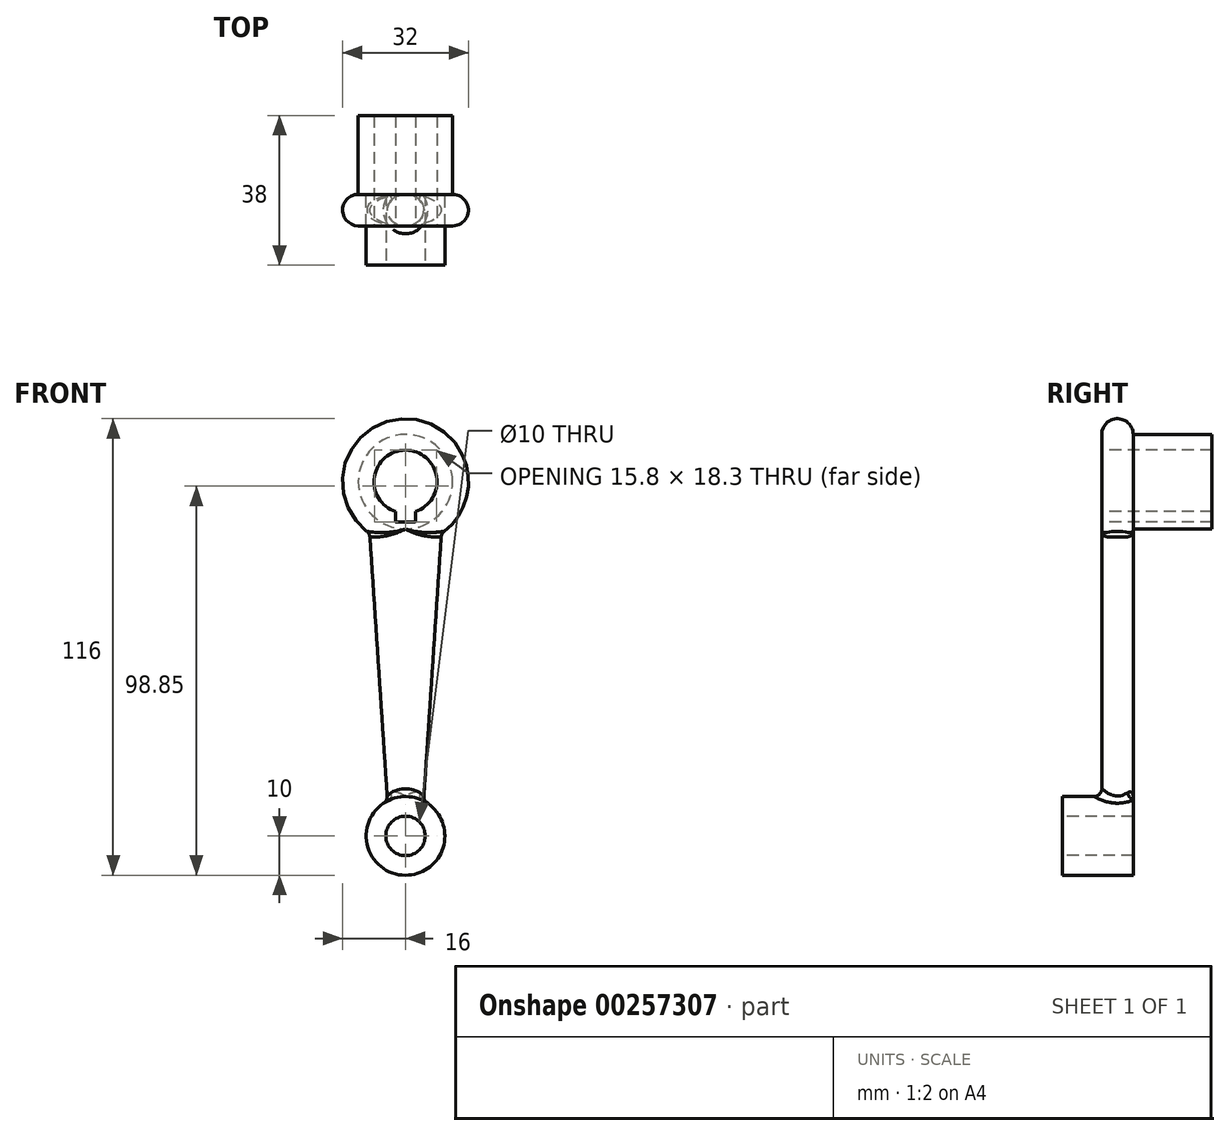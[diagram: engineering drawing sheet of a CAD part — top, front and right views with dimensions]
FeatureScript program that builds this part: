
annotation { "Feature Type Name" : "Feature", "Feature Type Description" : "" }
export const myFeature = defineFeature(function(context is Context, id is Id, definition is map)
    precondition{}
    {
        {
            var Q0;
            Q0=qCreatedBy(makeId("Right.planeOp"),FACE);
            var sketch = newSketch(context, id + "F0", { "sketchPlane" : qUnion([Q0])});
            skLineSegment(sketch, "E0", {"start": v(0, 8) * mm, "end": v(28, 8) * mm, "construction": true});
            skLineSegment(sketch, "E1", {"start": v(28, 8) * mm, "end": v(28, 12) * mm});
            skLineSegment(sketch, "E2", {"start": v(28, 12) * mm, "end": v(8, 12) * mm});
            skLineSegment(sketch, "E3", {"start": v(0, 12) * mm, "end": v(0, 8) * mm});
            skArc(sketch, "E4", {"start": v(0, 12) * mm, "mid": v(4, 16) * mm, "end": v(8, 12) * mm});
            skLineSegment(sketch, "E5", {"start": v(-3.82, 0) * mm, "end": v(31.7, 0) * mm, "construction": true});
            skLineSegment(sketch, "E6", {"start": v(0, 8) * mm, "end": v(0, 0) * mm});
            skLineSegment(sketch, "E7", {"start": v(0, 0) * mm, "end": v(28, 0) * mm});
            skLineSegment(sketch, "E8", {"start": v(28, 0) * mm, "end": v(28, 8) * mm});
            skSolve(sketch);
        }
        {
            var Q0;
            Q0=makeQuery(id+"F0.imprint","IMPRINT",FACE,{"disambiguationData":[TD([[makeQuery(id+"F0.imprint","IMPRINT",EDGE,{"derivedFrom":sQuery(id+"F0.wireOp",EDGE,"E1")}),1.0]])]});
            var Q1;
            Q1=sQuery(id+"F0.wireOp",EDGE,"E5");
            revolve(context, id + "F1", {"entities" : qUnion([Q0]), "axis" : qUnion([Q1]), "revolveType" : RevolveType.FULL});
        }
        {
            var Q0;
            Q0=qCreatedBy(makeId("Front.planeOp"),FACE);
            var sketch = newSketch(context, id + "F2", { "sketchPlane" : qUnion([Q0])});
            skCircle(sketch, "E9", {"center": v(0, -90) * mm, "radius": 10 * mm});
            skSolve(sketch);
        }
        {
            var Q0;
            Q0=makeQuery(id+"F2.imprint","IMPRINT",FACE,{"disambiguationData":[TD([[makeQuery(id+"F2.imprint","IMPRINT",EDGE,{"derivedFrom":sQuery(id+"F2.wireOp",EDGE,"E9")}),1.0]])]});
            extrude(context, id + "F3", {"entities" : qUnion([Q0]), "depth" : 10 * mm, "hasSecondDirection" : true, "secondDirectionOppositeDirection" : true, "secondDirectionDepth" : 8 * mm});
        }
        {
            var Q0;
            Q0=qCreatedBy(makeId("Front.planeOp"),FACE);
            cPlane(context, id + "F4", {"entities" : qUnion([Q0]), "cplaneType" : CPlaneType.OFFSET, "offset" : 4 * mm, "oppositeDirection" : true, "width" : 150 * mm, "height" : 150 * mm});
        }
        {
            var Q0;
            Q0=qCreatedBy(id+"F4.planeOp",FACE);
            var sketch = newSketch(context, id + "F5", { "sketchPlane" : qUnion([Q0])});
            skLineSegment(sketch, "E10", {"start": v(10, 0) * mm, "end": v(4, -90) * mm, "construction": true});
            skLineSegment(sketch, "E11.MirrorCS", {"start": v(-10, 0) * mm, "end": v(-4, -90) * mm, "construction": true});
            skCircle(sketch, "E12.0", {"center": v(0, -90) * mm, "radius": 10 * mm});
            skSolve(sketch);
        }
        {
            var Q0;
            Q0=qCreatedBy(makeId("Top.planeOp"),FACE);
            cPlane(context, id + "F6", {"entities" : qUnion([Q0]), "cplaneType" : CPlaneType.OFFSET, "offset" : 90 * mm, "oppositeDirection" : true, "width" : 150 * mm, "height" : 150 * mm});
        }
        {
            var Q0;
            Q0=qCreatedBy(makeId("Top.planeOp"),FACE);
            var sketch = newSketch(context, id + "F7", { "sketchPlane" : qUnion([Q0])});
            skPoint(sketch, "E13.0", {"position": v(10, 4) * mm});
            skPoint(sketch, "E13.1", {"position": v(-10, 4) * mm});
            skPoint(sketch, "E14.0", {"position": v(0, 4) * mm});
            skEllipse(sketch, "E15", {"center": v(0, 4) * mm, "majorRadius": 10 * mm, "minorRadius": 4 * mm, "majorAxis": v(1, 0)});
            skSolve(sketch);
        }
        {
            var Q0;
            Q0=qCreatedBy(id+"F6.planeOp",FACE);
            var sketch = newSketch(context, id + "F8", { "sketchPlane" : qUnion([Q0])});
            skPoint(sketch, "E16.0", {"position": v(0, 4) * mm});
            skPoint(sketch, "E16.1", {"position": v(-4, 4) * mm});
            skPoint(sketch, "E16.2", {"position": v(4, 4) * mm});
            skEllipse(sketch, "E17", {"center": v(0, 4) * mm, "majorRadius": 4 * mm, "minorRadius": 4 * mm, "majorAxis": v(-1, 0)});
            skSolve(sketch);
        }
        {
            var Q0;
            Q0 = qSketchRegion(id + "F7", true);
            var Q1;
            Q1 = qSketchRegion(id + "F8", true);
            loft(context, id + "F9", {"sheetProfilesArray" : [{ "sheetProfileEntities" : qUnion([Q0]) }, { "sheetProfileEntities" : qUnion([Q1]) }]});
        }
        {
            var Q0;
            Q0=makeQuery(id+"F1.opRevolve","SWEPT_BODY",BODY,{"disambiguationData":[OSD([sQuery(id+"F0.wireOp",EDGE,"E1"),sQuery(id+"F0.wireOp",EDGE,"E2"),sQuery(id+"F0.wireOp",EDGE,"E3"),sQuery(id+"F0.wireOp",EDGE,"E4"),sQuery(id+"F0.wireOp",EDGE,"E6"),sQuery(id+"F0.wireOp",EDGE,"E7"),sQuery(id+"F0.wireOp",EDGE,"E8")])]});
            var Q1;
            Q1=makeQuery(id+"F9.opLoft","SWEPT_BODY",BODY,{"disambiguationData":[OSD([makeQuery(id+"F7.imprint","IMPRINT",FACE,{"disambiguationData":[TD([[makeQuery(id+"F7.imprint","IMPRINT",EDGE,{"derivedFrom":sQuery(id+"F7.wireOp",EDGE,"E15")}),1.0]])]}),makeQuery(id+"F8.imprint","IMPRINT",FACE,{"disambiguationData":[TD([[makeQuery(id+"F8.imprint","IMPRINT",EDGE,{"derivedFrom":sQuery(id+"F8.wireOp",EDGE,"E17")}),1.0]])]})])]});
            var Q2;
            Q2=makeQuery(id+"F3.opExtrude","SWEPT_BODY",BODY,{"disambiguationData":[OSD([sQuery(id+"F2.wireOp",EDGE,"E9")])]});
            booleanBodies(context, id + "F10", {"operationType" : BooleanOperationType.UNION, "tools" : qUnion([Q0, Q1, Q2])});
        }
        {
            var Q0;
            Q0=makeQuery(id+"F1.opRevolve","SWEPT_FACE",FACE,{"disambiguationData":[OSD([sQuery(id+"F0.wireOp",EDGE,"E3"),sQuery(id+"F0.wireOp",EDGE,"E6")])]});
            var sketch = newSketch(context, id + "F11", { "sketchPlane" : qUnion([Q0])});
            skPoint(sketch, "E18", {"position": v(0, 0) * mm});
            skLineSegment(sketch, "E19.bottom", {"start": v(-2.5, -6) * mm, "end": v(2.5, -6) * mm});
            skLineSegment(sketch, "E19.top", {"start": v(-2.5, -10.3) * mm, "end": v(2.5, -10.3) * mm});
            skLineSegment(sketch, "E19.left", {"start": v(-2.5, -6) * mm, "end": v(-2.5, -10.3) * mm});
            skLineSegment(sketch, "E19.right", {"start": v(2.5, -6) * mm, "end": v(2.5, -10.3) * mm});
            skSolve(sketch);
        }
        {
            var Q0;
            Q0=sQuery(id+"F11.wireOp",VERTEX,"E18");
            var Q1;
            Q1=makeQuery(id+"F1.opRevolve","SWEPT_BODY",BODY,{"disambiguationData":[OSD([sQuery(id+"F0.wireOp",EDGE,"E1"),sQuery(id+"F0.wireOp",EDGE,"E2"),sQuery(id+"F0.wireOp",EDGE,"E3"),sQuery(id+"F0.wireOp",EDGE,"E4"),sQuery(id+"F0.wireOp",EDGE,"E6"),sQuery(id+"F0.wireOp",EDGE,"E7"),sQuery(id+"F0.wireOp",EDGE,"E8")])]});
            hole(context, id + "F12", {"style" : HoleStyle.SIMPLE, "endStyle" : HoleEndStyle.THROUGH, "holeDiameter" : 16 * mm, "tappedDepth" : 12 * mm, "tapClearance" : 3, "locations" : qUnion([Q0]), "scope" : qUnion([Q1])});
        }
        {
            var Q0;
            Q0=makeQuery(id+"F11.imprint","IMPRINT",FACE,{"disambiguationData":[TD([[makeQuery(id+"F11.imprint","IMPRINT",EDGE,{"derivedFrom":sQuery(id+"F11.wireOp",EDGE,"E19.bottom")}),-1.0]])]});
            extrude(context, id + "F13", {"entities" : qUnion([Q0]), "operationType" : NewBodyOperationType.REMOVE, "endBound" : BoundingType.THROUGH_ALL, "oppositeDirection" : true, "depth" : 25 * mm});
        }
        {
            var Q0;
            Q0=makeQuery(id+"F13.boolean.opBoolean","COPY",EDGE,{"derivedFrom":makeQuery(id+"F13.opExtrude","SWEPT_EDGE",EDGE,{"disambiguationData":[OSD([sQuery(id+"F11.wireOp",EDGE,"E19.top"),sQuery(id+"F11.wireOp",EDGE,"E19.left")])]})});
            var Q1;
            Q1=makeQuery(id+"F13.boolean.opBoolean","COPY",EDGE,{"derivedFrom":makeQuery(id+"F13.opExtrude","SWEPT_EDGE",EDGE,{"disambiguationData":[OSD([sQuery(id+"F11.wireOp",EDGE,"E19.top"),sQuery(id+"F11.wireOp",EDGE,"E19.right")])]})});
            fillet(context, id + "F14", {"entities" : qUnion([Q0, Q1]), "radius" : 0.2 * mm, "tangentPropagation" : true, "allowEdgeOverflow" : false});
        }
        {
            var Q0;
            Q0=makeQuery(id+"F3.opExtrude","CAP_FACE",FACE,{"disambiguationData":[OSD([sQuery(id+"F2.wireOp",EDGE,"E9")])],"isStart":false});
            var sketch = newSketch(context, id + "F15", { "sketchPlane" : qUnion([Q0])});
            skPoint(sketch, "E20", {"position": v(0, -90) * mm});
            skSolve(sketch);
        }
        {
            var Q0;
            Q0=sQuery(id+"F15.wireOp",VERTEX,"E20");
            var Q1;
            Q1=makeQuery(id+"F1.opRevolve","SWEPT_BODY",BODY,{"disambiguationData":[OSD([sQuery(id+"F0.wireOp",EDGE,"E1"),sQuery(id+"F0.wireOp",EDGE,"E2"),sQuery(id+"F0.wireOp",EDGE,"E3"),sQuery(id+"F0.wireOp",EDGE,"E4"),sQuery(id+"F0.wireOp",EDGE,"E6"),sQuery(id+"F0.wireOp",EDGE,"E7"),sQuery(id+"F0.wireOp",EDGE,"E8")])]});
            hole(context, id + "F16", {"style" : HoleStyle.SIMPLE, "endStyle" : HoleEndStyle.THROUGH, "holeDiameter" : 10 * mm, "tappedDepth" : 12 * mm, "tapClearance" : 3, "locations" : qUnion([Q0]), "scope" : qUnion([Q1])});
        }
        {
            var Q0;
            Q0=makeQuery(id+"F10.opBoolean","INTERSECT",EDGE,{"disambiguationData":[OD(1.0)],"derivedFrom":[makeQuery(id+"F1.opRevolve","SWEPT_FACE",FACE,{"disambiguationData":[OSD([sQuery(id+"F0.wireOp",EDGE,"E4")])]}),makeQuery(id+"F9.opLoft","SWEPT_FACE",FACE,{"disambiguationData":[OSD([sQuery(id+"F7.wireOp",EDGE,"E15"),sQuery(id+"F8.wireOp",EDGE,"E17")])]})]});
            var Q1;
            Q1=makeQuery(id+"F10.opBoolean","INTERSECT",EDGE,{"derivedFrom":[makeQuery(id+"F3.opExtrude","SWEPT_FACE",FACE,{"disambiguationData":[OSD([sQuery(id+"F2.wireOp",EDGE,"E9")])]}),makeQuery(id+"F9.opLoft","SWEPT_FACE",FACE,{"disambiguationData":[OSD([sQuery(id+"F7.wireOp",EDGE,"E15"),sQuery(id+"F8.wireOp",EDGE,"E17")])]})]});
            var Q2;
            Q2=makeQuery(id+"F10.opBoolean","INTERSECT",EDGE,{"disambiguationData":[OD(0.0)],"derivedFrom":[makeQuery(id+"F1.opRevolve","SWEPT_FACE",FACE,{"disambiguationData":[OSD([sQuery(id+"F0.wireOp",EDGE,"E4")])]}),makeQuery(id+"F9.opLoft","SWEPT_FACE",FACE,{"disambiguationData":[OSD([sQuery(id+"F7.wireOp",EDGE,"E15"),sQuery(id+"F8.wireOp",EDGE,"E17")])]})]});
            fillet(context, id + "F17", {"entities" : qUnion([Q0, Q1, Q2]), "radius" : 2 * mm, "tangentPropagation" : true, "allowEdgeOverflow" : false});
        }
    });
